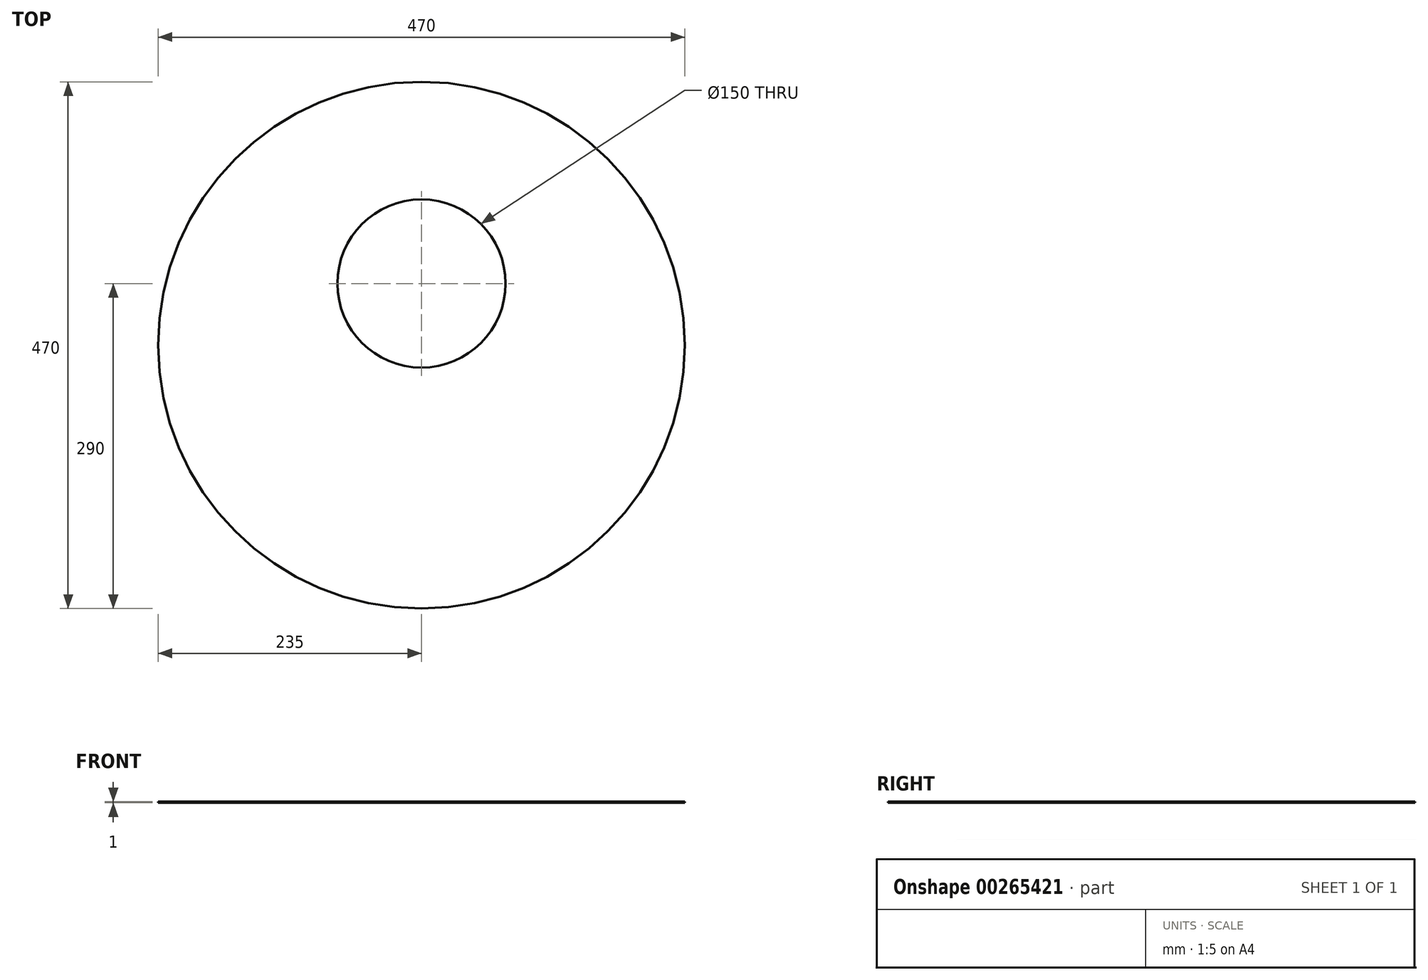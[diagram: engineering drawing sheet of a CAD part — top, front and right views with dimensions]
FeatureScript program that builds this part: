
annotation { "Feature Type Name" : "Feature", "Feature Type Description" : "" }
export const myFeature = defineFeature(function(context is Context, id is Id, definition is map)
    precondition{}
    {
        {
            var Q0;
            Q0=qCreatedBy(makeId("Front.planeOp"),FACE);
            var sketch = newSketch(context, id + "F0", { "sketchPlane" : qUnion([Q0])});
            skLineSegment(sketch, "E0", {"start": v(0, 0) * mm, "end": v(-235, 0) * mm});
            skLineSegment(sketch, "E1", {"start": v(-235, 110) * mm, "end": v(0, 110) * mm});
            skLineSegment(sketch, "E2", {"start": v(-235, 0) * mm, "end": v(-235, 110) * mm});
            skLineSegment(sketch, "E3", {"start": v(0, 110) * mm, "end": v(0, 0) * mm});
            skSolve(sketch);
        }
        {
            var Q0;
            Q0=makeQuery(id+"F0.imprint","IMPRINT",FACE,{"disambiguationData":[TD([[makeQuery(id+"F0.imprint","IMPRINT",EDGE,{"derivedFrom":sQuery(id+"F0.wireOp",EDGE,"E0")}),-1.0]])]});
            var Q1;
            Q1=sQuery(id+"F0.wireOp",EDGE,"E3");
            revolve(context, id + "F1", {"entities" : qUnion([Q0]), "axis" : qUnion([Q1]), "revolveType" : RevolveType.FULL});
        }
        {
            var Q0;
            Q0=makeQuery(id+"F1.opRevolve","SWEPT_FACE",FACE,{"disambiguationData":[OSD([sQuery(id+"F0.wireOp",EDGE,"E0")])]});
            shell(context, id + "F2", {"entities" : qUnion([Q0]), "thickness" : 1 * mm});
        }
        {
            var Q0;
            Q0=makeQuery(id+"F1.opRevolve","SWEPT_FACE",FACE,{"disambiguationData":[OSD([sQuery(id+"F0.wireOp",EDGE,"E1")])]});
            var sketch = newSketch(context, id + "F3", { "sketchPlane" : qUnion([Q0])});
            skLineSegment(sketch, "E4", {"start": v(0, 235) * mm, "end": v(0, 55) * mm});
            skCircle(sketch, "E5", {"center": v(0, 55) * mm, "radius": 140 * mm});
            skCircle(sketch, "E6.0", {"center": v(0, 55) * mm, "radius": 75 * mm});
            skSolve(sketch);
        }
        {
            var Q0;
            Q0=makeQuery(id+"F3.imprint","IMPRINT",FACE,{"disambiguationData":[TD([[makeQuery(id+"F3.imprint","IMPRINT",EDGE,{"derivedFrom":sQuery(id+"F3.wireOp",EDGE,"E5")}),-1.0]])]});
            var Q1;
            Q1=makeQuery(id+"F3.imprint","IMPRINT",FACE,{"disambiguationData":[TD([[makeQuery(id+"F3.imprint","IMPRINT",EDGE,{"derivedFrom":sQuery(id+"F3.wireOp",EDGE,"E5")}),1.0]])]});
            extrude(context, id + "F4", {"entities" : qUnion([Q0, Q1]), "depth" : 1 * mm});
        }
        {
            var Q0;
            Q0=makeQuery(id+"F1.opRevolve","SWEPT_BODY",BODY,{"disambiguationData":[OSD([sQuery(id+"F0.wireOp",EDGE,"E0"),sQuery(id+"F0.wireOp",EDGE,"E1"),sQuery(id+"F0.wireOp",EDGE,"E2"),sQuery(id+"F0.wireOp",EDGE,"E3")])]});
            deleteBodies(context, id + "F5", {"entities" : qUnion([Q0])});
        }
    });
